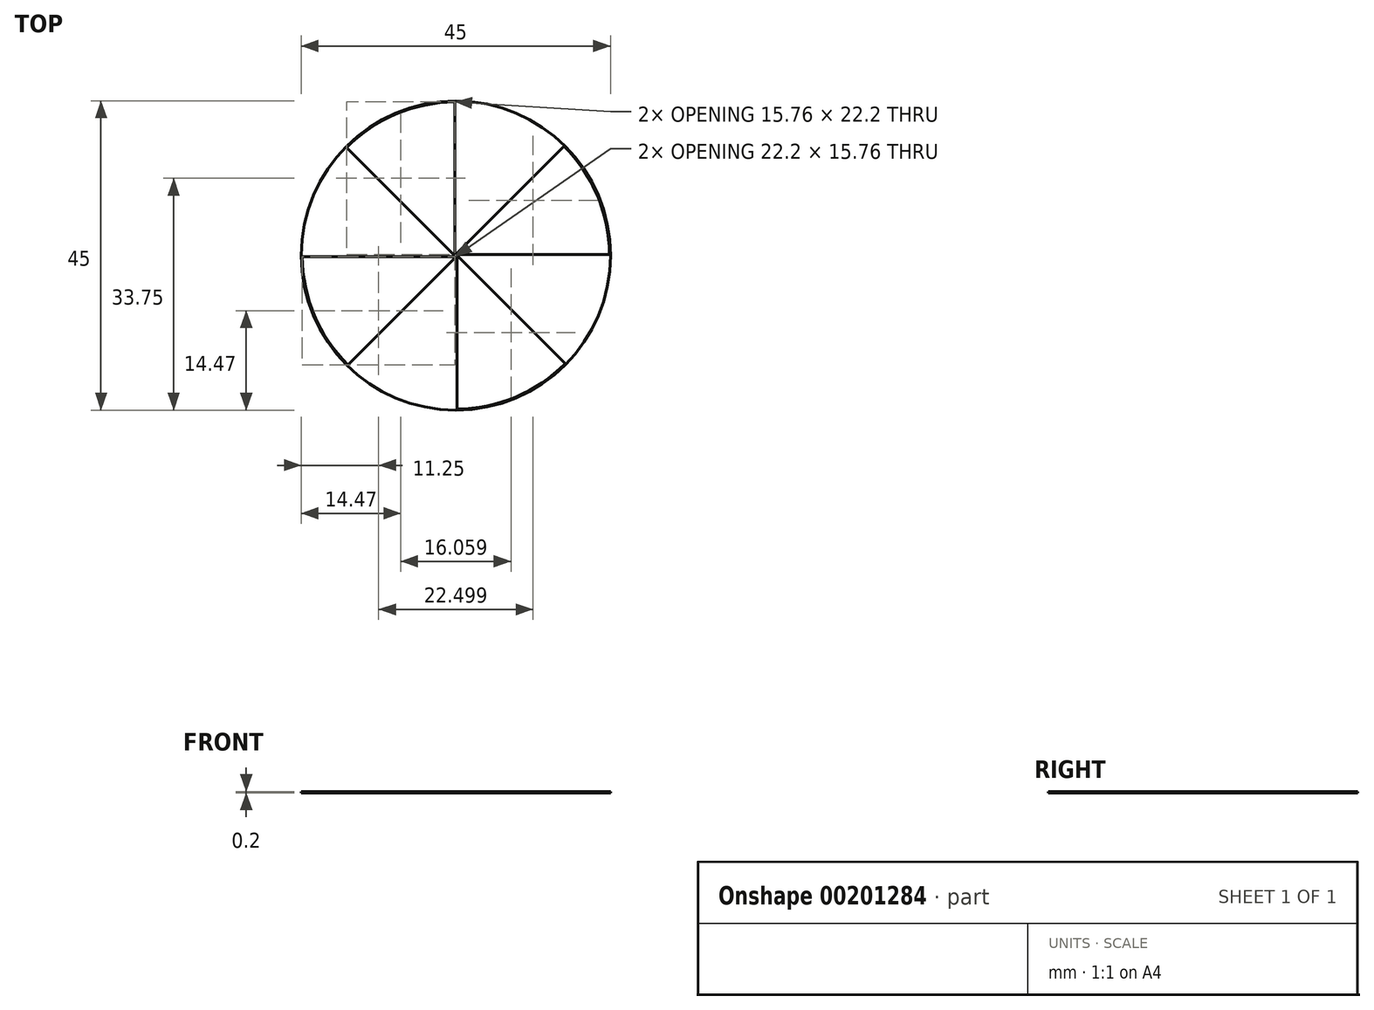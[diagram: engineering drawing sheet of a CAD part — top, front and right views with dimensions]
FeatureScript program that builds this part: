
annotation { "Feature Type Name" : "Feature", "Feature Type Description" : "" }
export const myFeature = defineFeature(function(context is Context, id is Id, definition is map)
    precondition{}
    {
        {
            var Q0;
            Q0=qCreatedBy(makeId("Top.planeOp"),FACE);
            var sketch = newSketch(context, id + "F0", { "sketchPlane" : qUnion([Q0])});
            skCircle(sketch, "E0", {"center": v(0, 0) * mm, "radius": 22.5 * mm});
            skCircle(sketch, "E1", {"center": v(0, 0) * mm, "radius": 22.35 * mm});
            skLineSegment(sketch, "E2", {"start": v(0, 0) * mm, "end": v(22.35, 0) * mm, "construction": true});
            skLineSegment(sketch, "E3", {"start": v(0, 0) * mm, "end": v(0, -22.5) * mm, "construction": true});
            skLineSegment(sketch, "E4", {"start": v(0, 0) * mm, "end": v(-22.35, 0) * mm, "construction": true});
            skLineSegment(sketch, "E5", {"start": v(-15.8, -15.8) * mm, "end": v(15.8, 15.8) * mm, "construction": true});
            skLineSegment(sketch, "E6", {"start": v(15.8, -15.8) * mm, "end": v(-15.8, 15.8) * mm, "construction": true});
            skLineSegment(sketch, "E7.0", {"start": v(15.9, -15.7) * mm, "end": v(-15.7, 15.9) * mm});
            skLineSegment(sketch, "E8.0", {"start": v(15.7, -15.9) * mm, "end": v(-15.9, 15.7) * mm});
            skLineSegment(sketch, "E9.0", {"start": v(0.15, 0) * mm, "end": v(0.15, 22.35) * mm});
            skLineSegment(sketch, "E10.0", {"start": v(0, 0) * mm, "end": v(0, 22.35) * mm, "construction": true});
            skLineSegment(sketch, "E11.0", {"start": v(-15.7, -15.9) * mm, "end": v(15.9, 15.7) * mm});
            skLineSegment(sketch, "E12.0", {"start": v(-15.9, -15.7) * mm, "end": v(15.7, 15.9) * mm});
            skLineSegment(sketch, "E13.0", {"start": v(0, -0.15) * mm, "end": v(22.35, -0.15) * mm});
            skLineSegment(sketch, "E14.0", {"start": v(0, 0.15) * mm, "end": v(22.35, 0.15) * mm});
            skLineSegment(sketch, "E15.0", {"start": v(-0.15, 0) * mm, "end": v(-0.15, -22.5) * mm});
            skLineSegment(sketch, "E16.0", {"start": v(0.15, 0) * mm, "end": v(0.15, -22.5) * mm});
            skLineSegment(sketch, "E17.0", {"start": v(0, 0.15) * mm, "end": v(-22.35, 0.15) * mm});
            skLineSegment(sketch, "E18.0", {"start": v(0, -0.15) * mm, "end": v(-22.35, -0.15) * mm});
            skLineSegment(sketch, "E19.0", {"start": v(-0.15, 0) * mm, "end": v(-0.15, 22.35) * mm});
            skSolve(sketch);
        }
        {
            var Q0;
            {var subQ10=sQuery(id+"F0.wireOp",EDGE,"E7.0");var subQ21=sQuery(id+"F0.wireOp",EDGE,"E9.0");var subQ22=makeQuery(id+"F0.imprint","INTERSECT",VERTEX,{"derivedFrom":[subQ10,subQ21]});Q0=makeQuery(id+"F0.imprint","IMPRINT",FACE,{"disambiguationData":[TD([[makeQuery(id+"F0.imprint","IMPRINT",EDGE,{"disambiguationData":[TD([[subQ22,-1.0]])],"derivedFrom":subQ10}),1.0]])]});}
            var Q1;
            {var subQ0=sQuery(id+"F0.wireOp",EDGE,"E14.0");var subQ1=sQuery(id+"F0.wireOp",EDGE,"E7.0");var subQ2=makeQuery(id+"F0.imprint","INTERSECT",VERTEX,{"derivedFrom":[subQ1,subQ0]});Q1=makeQuery(id+"F0.imprint","IMPRINT",FACE,{"disambiguationData":[TD([[makeQuery(id+"F0.imprint","IMPRINT",EDGE,{"disambiguationData":[TD([[subQ2,-1.0]])],"derivedFrom":subQ1}),1.0]])]});}
            var Q2;
            {var subQ0=sQuery(id+"F0.wireOp",EDGE,"E11.0");var subQ1=sQuery(id+"F0.wireOp",EDGE,"E7.0");var subQ2=makeQuery(id+"F0.imprint","INTERSECT",VERTEX,{"derivedFrom":[subQ1,subQ0]});Q2=makeQuery(id+"F0.imprint","IMPRINT",FACE,{"disambiguationData":[TD([[makeQuery(id+"F0.imprint","IMPRINT",EDGE,{"disambiguationData":[TD([[subQ2,-1.0]])],"derivedFrom":subQ1}),1.0]])]});}
            var Q3;
            {var subQ0=sQuery(id+"F0.wireOp",EDGE,"E13.0");var subQ1=sQuery(id+"F0.wireOp",EDGE,"E11.0");var subQ2=makeQuery(id+"F0.imprint","INTERSECT",VERTEX,{"derivedFrom":[subQ1,subQ0]});Q3=makeQuery(id+"F0.imprint","IMPRINT",FACE,{"disambiguationData":[TD([[makeQuery(id+"F0.imprint","IMPRINT",EDGE,{"disambiguationData":[TD([[subQ2,-1.0]])],"derivedFrom":subQ1}),-1.0]])]});}
            var Q4;
            {var subQ0=sQuery(id+"F0.wireOp",EDGE,"E9.0");var subQ1=sQuery(id+"F0.wireOp",EDGE,"E7.0");var subQ2=makeQuery(id+"F0.imprint","INTERSECT",VERTEX,{"derivedFrom":[subQ1,subQ0]});Q4=makeQuery(id+"F0.imprint","IMPRINT",FACE,{"disambiguationData":[TD([[makeQuery(id+"F0.imprint","IMPRINT",EDGE,{"disambiguationData":[TD([[subQ2,-1.0]])],"derivedFrom":subQ1}),-1.0]])]});}
            var Q5;
            {var subQ0=sQuery(id+"F0.wireOp",EDGE,"E11.0");var subQ1=sQuery(id+"F0.wireOp",EDGE,"E7.0");var subQ2=makeQuery(id+"F0.imprint","INTERSECT",VERTEX,{"derivedFrom":[subQ1,subQ0]});Q5=makeQuery(id+"F0.imprint","IMPRINT",FACE,{"disambiguationData":[TD([[makeQuery(id+"F0.imprint","IMPRINT",EDGE,{"disambiguationData":[TD([[subQ2,-1.0]])],"derivedFrom":subQ1}),-1.0]])]});}
            var Q6;
            {var subQ0=sQuery(id+"F0.wireOp",EDGE,"E14.0");var subQ1=sQuery(id+"F0.wireOp",EDGE,"E7.0");var subQ2=makeQuery(id+"F0.imprint","INTERSECT",VERTEX,{"derivedFrom":[subQ1,subQ0]});Q6=makeQuery(id+"F0.imprint","IMPRINT",FACE,{"disambiguationData":[TD([[makeQuery(id+"F0.imprint","IMPRINT",EDGE,{"disambiguationData":[TD([[subQ2,-1.0]])],"derivedFrom":subQ1}),-1.0]])]});}
            var Q7;
            {var subQ0=sQuery(id+"F0.wireOp",EDGE,"E13.0");var subQ1=sQuery(id+"F0.wireOp",EDGE,"E7.0");var subQ2=makeQuery(id+"F0.imprint","INTERSECT",VERTEX,{"derivedFrom":[subQ1,subQ0]});Q7=makeQuery(id+"F0.imprint","IMPRINT",FACE,{"disambiguationData":[TD([[makeQuery(id+"F0.imprint","IMPRINT",EDGE,{"disambiguationData":[TD([[subQ2,-1.0]])],"derivedFrom":subQ1}),1.0]])]});}
            var Q8;
            {var subQ3=sQuery(id+"F0.wireOp",EDGE,"E14.0");var subQ7=sQuery(id+"F0.wireOp",EDGE,"E1");var subQ8=makeQuery(id+"F0.imprint","INTERSECT",VERTEX,{"derivedFrom":[subQ7,subQ3]});Q8=makeQuery(id+"F0.imprint","IMPRINT",FACE,{"disambiguationData":[TD([[makeQuery(id+"F0.imprint","IMPRINT",EDGE,{"disambiguationData":[TD([[subQ8,1.0]])],"derivedFrom":subQ7}),1.0]])]});}
            var Q9;
            {var subQ0=sQuery(id+"F0.wireOp",EDGE,"E11.0");var subQ1=sQuery(id+"F0.wireOp",EDGE,"E1");var subQ2=makeQuery(id+"F0.imprint","INTERSECT",VERTEX,{"disambiguationData":[OD(0.0)],"derivedFrom":[subQ1,subQ0]});Q9=makeQuery(id+"F0.imprint","IMPRINT",FACE,{"disambiguationData":[TD([[makeQuery(id+"F0.imprint","IMPRINT",EDGE,{"disambiguationData":[TD([[subQ2,-1.0]])],"derivedFrom":subQ1}),1.0]])]});}
            var Q10;
            {var subQ3=sQuery(id+"F0.wireOp",EDGE,"E9.0");var subQ7=sQuery(id+"F0.wireOp",EDGE,"E1");var subQ8=makeQuery(id+"F0.imprint","INTERSECT",VERTEX,{"derivedFrom":[subQ7,subQ3]});Q10=makeQuery(id+"F0.imprint","IMPRINT",FACE,{"disambiguationData":[TD([[makeQuery(id+"F0.imprint","IMPRINT",EDGE,{"disambiguationData":[TD([[subQ8,-1.0]])],"derivedFrom":subQ7}),1.0]])]});}
            var Q11;
            {var subQ0=sQuery(id+"F0.wireOp",EDGE,"E16.0");var subQ1=sQuery(id+"F0.wireOp",EDGE,"E8.0");var subQ2=makeQuery(id+"F0.imprint","INTERSECT",VERTEX,{"derivedFrom":[subQ1,subQ0]});Q11=makeQuery(id+"F0.imprint","IMPRINT",FACE,{"disambiguationData":[TD([[makeQuery(id+"F0.imprint","IMPRINT",EDGE,{"disambiguationData":[TD([[subQ2,-1.0]])],"derivedFrom":subQ1}),-1.0]])]});}
            var Q12;
            {var subQ5=sQuery(id+"F0.wireOp",EDGE,"E8.0");var subQ6=sQuery(id+"F0.wireOp",EDGE,"E1");var subQ7=makeQuery(id+"F0.imprint","INTERSECT",VERTEX,{"disambiguationData":[OD(1.0)],"derivedFrom":[subQ6,subQ5]});Q12=makeQuery(id+"F0.imprint","IMPRINT",FACE,{"disambiguationData":[TD([[makeQuery(id+"F0.imprint","IMPRINT",EDGE,{"disambiguationData":[TD([[subQ7,-1.0]])],"derivedFrom":subQ6}),1.0]])]});}
            var Q13;
            {var subQ0=sQuery(id+"F0.wireOp",EDGE,"E11.0");var subQ1=sQuery(id+"F0.wireOp",EDGE,"E8.0");var subQ2=makeQuery(id+"F0.imprint","INTERSECT",VERTEX,{"derivedFrom":[subQ1,subQ0]});Q13=makeQuery(id+"F0.imprint","IMPRINT",FACE,{"disambiguationData":[TD([[makeQuery(id+"F0.imprint","IMPRINT",EDGE,{"disambiguationData":[TD([[subQ2,-1.0]])],"derivedFrom":subQ1}),-1.0]])]});}
            var Q14;
            {var subQ0=sQuery(id+"F0.wireOp",EDGE,"E11.0");var subQ1=sQuery(id+"F0.wireOp",EDGE,"E8.0");var subQ2=makeQuery(id+"F0.imprint","INTERSECT",VERTEX,{"derivedFrom":[subQ1,subQ0]});Q14=makeQuery(id+"F0.imprint","IMPRINT",FACE,{"disambiguationData":[TD([[makeQuery(id+"F0.imprint","IMPRINT",EDGE,{"disambiguationData":[TD([[subQ2,-1.0]])],"derivedFrom":subQ1}),1.0]])]});}
            var Q15;
            {var subQ0=sQuery(id+"F0.wireOp",EDGE,"E18.0");var subQ1=sQuery(id+"F0.wireOp",EDGE,"E8.0");var subQ2=makeQuery(id+"F0.imprint","INTERSECT",VERTEX,{"derivedFrom":[subQ1,subQ0]});Q15=makeQuery(id+"F0.imprint","IMPRINT",FACE,{"disambiguationData":[TD([[makeQuery(id+"F0.imprint","IMPRINT",EDGE,{"disambiguationData":[TD([[subQ2,-1.0]])],"derivedFrom":subQ1}),1.0]])]});}
            var Q16;
            {var subQ0=sQuery(id+"F0.wireOp",EDGE,"E15.0");var subQ1=sQuery(id+"F0.wireOp",EDGE,"E8.0");var subQ2=makeQuery(id+"F0.imprint","INTERSECT",VERTEX,{"derivedFrom":[subQ1,subQ0]});Q16=makeQuery(id+"F0.imprint","IMPRINT",FACE,{"disambiguationData":[TD([[makeQuery(id+"F0.imprint","IMPRINT",EDGE,{"disambiguationData":[TD([[subQ2,-1.0]])],"derivedFrom":subQ1}),-1.0]])]});}
            var Q17;
            {var subQ0=sQuery(id+"F0.wireOp",EDGE,"E12.0");var subQ1=sQuery(id+"F0.wireOp",EDGE,"E7.0");var subQ2=makeQuery(id+"F0.imprint","INTERSECT",VERTEX,{"derivedFrom":[subQ1,subQ0]});Q17=makeQuery(id+"F0.imprint","IMPRINT",FACE,{"disambiguationData":[TD([[makeQuery(id+"F0.imprint","IMPRINT",EDGE,{"disambiguationData":[TD([[subQ2,-1.0]])],"derivedFrom":subQ1}),1.0]])]});}
            var Q18;
            {var subQ0=sQuery(id+"F0.wireOp",EDGE,"E19.0");var subQ1=sQuery(id+"F0.wireOp",EDGE,"E12.0");var subQ2=makeQuery(id+"F0.imprint","INTERSECT",VERTEX,{"derivedFrom":[subQ1,subQ0]});Q18=makeQuery(id+"F0.imprint","IMPRINT",FACE,{"disambiguationData":[TD([[makeQuery(id+"F0.imprint","IMPRINT",EDGE,{"disambiguationData":[TD([[subQ2,-1.0]])],"derivedFrom":subQ1}),1.0]])]});}
            var Q19;
            {var subQ0=sQuery(id+"F0.wireOp",EDGE,"E12.0");var subQ1=sQuery(id+"F0.wireOp",EDGE,"E8.0");var subQ2=makeQuery(id+"F0.imprint","INTERSECT",VERTEX,{"derivedFrom":[subQ1,subQ0]});Q19=makeQuery(id+"F0.imprint","IMPRINT",FACE,{"disambiguationData":[TD([[makeQuery(id+"F0.imprint","IMPRINT",EDGE,{"disambiguationData":[TD([[subQ2,-1.0]])],"derivedFrom":subQ1}),-1.0]])]});}
            var Q20;
            {var subQ5=sQuery(id+"F0.wireOp",EDGE,"E7.0");var subQ6=sQuery(id+"F0.wireOp",EDGE,"E1");var subQ7=makeQuery(id+"F0.imprint","INTERSECT",VERTEX,{"disambiguationData":[OD(0.0)],"derivedFrom":[subQ6,subQ5]});Q20=makeQuery(id+"F0.imprint","IMPRINT",FACE,{"disambiguationData":[TD([[makeQuery(id+"F0.imprint","IMPRINT",EDGE,{"disambiguationData":[TD([[subQ7,-1.0]])],"derivedFrom":subQ6}),1.0]])]});}
            var Q21;
            {var subQ0=sQuery(id+"F0.wireOp",EDGE,"E17.0");var subQ1=sQuery(id+"F0.wireOp",EDGE,"E1");var subQ2=makeQuery(id+"F0.imprint","INTERSECT",VERTEX,{"derivedFrom":[subQ1,subQ0]});Q21=makeQuery(id+"F0.imprint","IMPRINT",FACE,{"disambiguationData":[TD([[makeQuery(id+"F0.imprint","IMPRINT",EDGE,{"disambiguationData":[TD([[subQ2,-1.0]])],"derivedFrom":subQ1}),1.0]])]});}
            var Q22;
            {var subQ0=sQuery(id+"F0.wireOp",EDGE,"E15.0");var subQ1=sQuery(id+"F0.wireOp",EDGE,"E8.0");var subQ2=makeQuery(id+"F0.imprint","INTERSECT",VERTEX,{"derivedFrom":[subQ1,subQ0]});Q22=makeQuery(id+"F0.imprint","IMPRINT",FACE,{"disambiguationData":[TD([[makeQuery(id+"F0.imprint","IMPRINT",EDGE,{"disambiguationData":[TD([[subQ2,-1.0]])],"derivedFrom":subQ1}),1.0]])]});}
            var Q23;
            {var subQ5=sQuery(id+"F0.wireOp",EDGE,"E12.0");var subQ6=sQuery(id+"F0.wireOp",EDGE,"E1");var subQ7=makeQuery(id+"F0.imprint","INTERSECT",VERTEX,{"disambiguationData":[OD(1.0)],"derivedFrom":[subQ6,subQ5]});Q23=makeQuery(id+"F0.imprint","IMPRINT",FACE,{"disambiguationData":[TD([[makeQuery(id+"F0.imprint","IMPRINT",EDGE,{"disambiguationData":[TD([[subQ7,-1.0]])],"derivedFrom":subQ6}),1.0]])]});}
            var Q24;
            {var subQ0=sQuery(id+"F0.wireOp",EDGE,"E15.0");var subQ1=sQuery(id+"F0.wireOp",EDGE,"E1");var subQ2=makeQuery(id+"F0.imprint","INTERSECT",VERTEX,{"derivedFrom":[subQ1,subQ0]});Q24=makeQuery(id+"F0.imprint","IMPRINT",FACE,{"disambiguationData":[TD([[makeQuery(id+"F0.imprint","IMPRINT",EDGE,{"disambiguationData":[TD([[subQ2,-1.0]])],"derivedFrom":subQ1}),1.0]])]});}
            var Q25;
            {var subQ0=sQuery(id+"F0.wireOp",EDGE,"E15.0");var subQ1=sQuery(id+"F0.wireOp",EDGE,"E0");var subQ2=makeQuery(id+"F0.imprint","INTERSECT",VERTEX,{"derivedFrom":[subQ1,subQ0]});Q25=makeQuery(id+"F0.imprint","IMPRINT",FACE,{"disambiguationData":[TD([[makeQuery(id+"F0.imprint","IMPRINT",EDGE,{"disambiguationData":[TD([[subQ2,-1.0]])],"derivedFrom":subQ1}),1.0]])]});}
            var Q26;
            {var subQ10=sQuery(id+"F0.wireOp",EDGE,"E15.0");var subQ11=sQuery(id+"F0.wireOp",EDGE,"E0");var subQ12=makeQuery(id+"F0.imprint","INTERSECT",VERTEX,{"derivedFrom":[subQ11,subQ10]});Q26=makeQuery(id+"F0.imprint","IMPRINT",FACE,{"disambiguationData":[TD([[makeQuery(id+"F0.imprint","IMPRINT",EDGE,{"disambiguationData":[TD([[subQ12,1.0]])],"derivedFrom":subQ11}),1.0]])]});}
            extrude(context, id + "F1", {"entities" : qUnion([Q0, Q1, Q2, Q3, Q4, Q5, Q6, Q7, Q8, Q9, Q10, Q11, Q12, Q13, Q14, Q15, Q16, Q17, Q18, Q19, Q20, Q21, Q22, Q23, Q24, Q25, Q26]), "depth" : .20 * mm});
        }
    });
